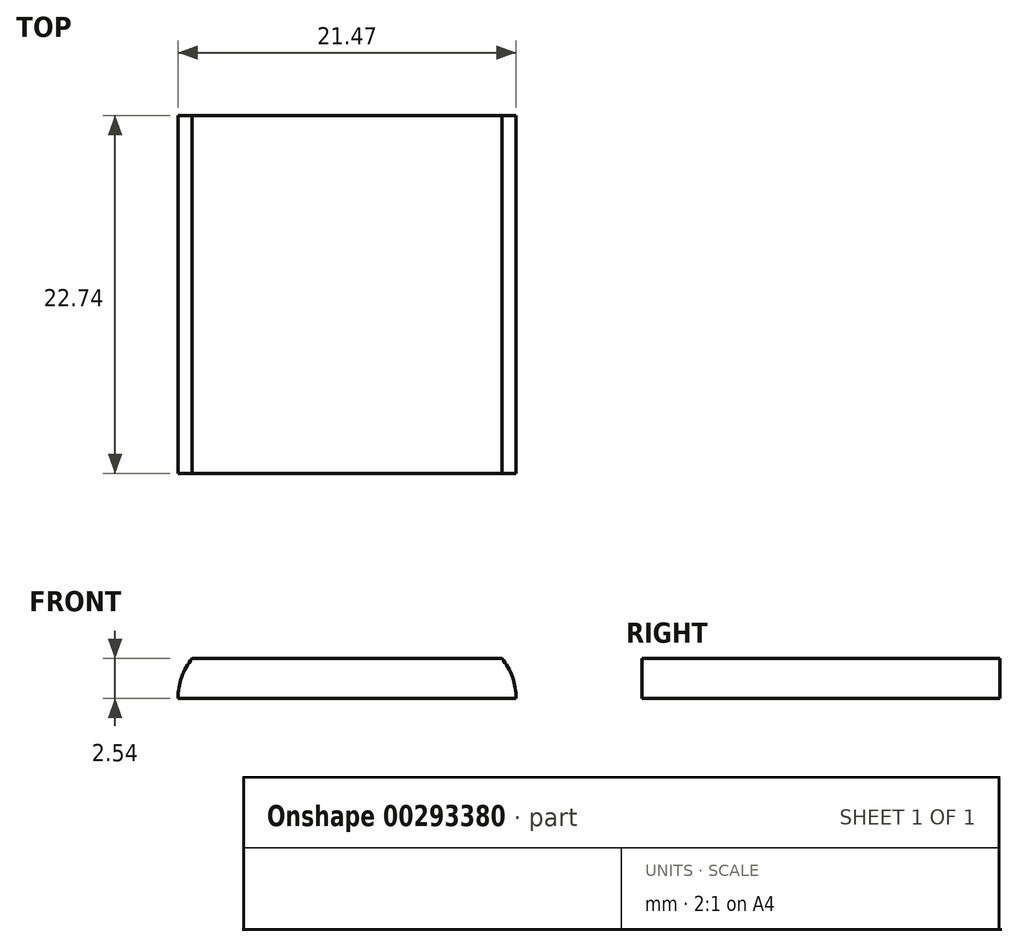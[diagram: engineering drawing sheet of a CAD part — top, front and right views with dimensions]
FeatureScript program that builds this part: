
annotation { "Feature Type Name" : "Feature", "Feature Type Description" : "" }
export const myFeature = defineFeature(function(context is Context, id is Id, definition is map)
    precondition{}
    {
        {
            var Q0;
            Q0=qCreatedBy(makeId("Front.planeOp"),FACE);
            var sketch = newSketch(context, id + "F0", { "sketchPlane" : qUnion([Q0])});
            skLineSegment(sketch, "E0", {"start": v(10.42, -1.3) * mm, "end": v(-11.05, -1.3) * mm});
            skLineSegment(sketch, "E1", {"start": v(-10.16, 1.24) * mm, "end": v(9.52, 1.24) * mm});
            skArc(sketch, "E2", {"start": v(-10.16, 1.24) * mm, "mid": v(-10.82, 0.05) * mm, "end": v(-11.05, -1.3) * mm});
            skArc(sketch, "E3", {"start": v(10.42, -1.3) * mm, "mid": v(10.2, 0.05) * mm, "end": v(9.52, 1.24) * mm});
            skSolve(sketch);
        }
        {
            var Q0;
            Q0=makeQuery(id+"F0.imprint","IMPRINT",FACE,{"disambiguationData":[TD([[makeQuery(id+"F0.imprint","IMPRINT",EDGE,{"derivedFrom":sQuery(id+"F0.wireOp",EDGE,"E0")}),-1.0]])]});
            extrude(context, id + "F1", {"entities" : qUnion([Q0]), "endBound" : BoundingType.SYMMETRIC, "depth" : 22.73 * mm});
        }
    });
